# Revit family: Specialty_Equipment-Fiberstone_Planter-Stone_Yard-Nagano
name_source: partatom
category: Specialty Equipment
units: mm (PartAtom-declared; Revit-internal decimal feet)

## family parameters
Always vertical = Yes
Cut with Voids When Loaded = No
Enable Cutting in Views = No
Maintain Annotation Orientation = No
OmniClass Number = 23.40.05.21.17
OmniClass Title = Planters
Part Type = Normal
Room Calculation Point = No
Round Connector Dimension = Use Diameter
Shared = No
Work Plane-Based = No

## types (3) — shared parameters
Assembly Code = G2050600
CD_Finish = Concrete-Fiberstone-Carlsbad-Fossil
CD_Inner Hole = 2.0"
CD_Microsite = https://www.caddetails.com
CD_Product Page URL = https://stoneyardinc.com
CD_Specification = https://stoneyardinc.com
Default Elevation = 0.0"
Description = Nagano Planter
Manufacturer = Stone Yard
Model = Nagano Planter
Type Comments = Round Planter
URL = https://stoneyardinc.com

## per-type parameters (varying)
| type | CD_Base Diameter | CD_Diameter | CD_Fillet Height | CD_Height | CD_Sides Length |
| 21"Dia x 16"H | 7.0" | 21.0" | 6.4" | 16.0" | 8.6" |
| 26"Dia x 20"H | 8.7" | 26.0" | 8.0" | 20.0" | 10.7" |
| 34"Dia x 28"H | 11.3" | 34.0" | 11.2" | 28.0" | 13.9" |

## geometry (parser evidence)
native form markers: Sweep x3
no freeform markers — native parametric forms only
